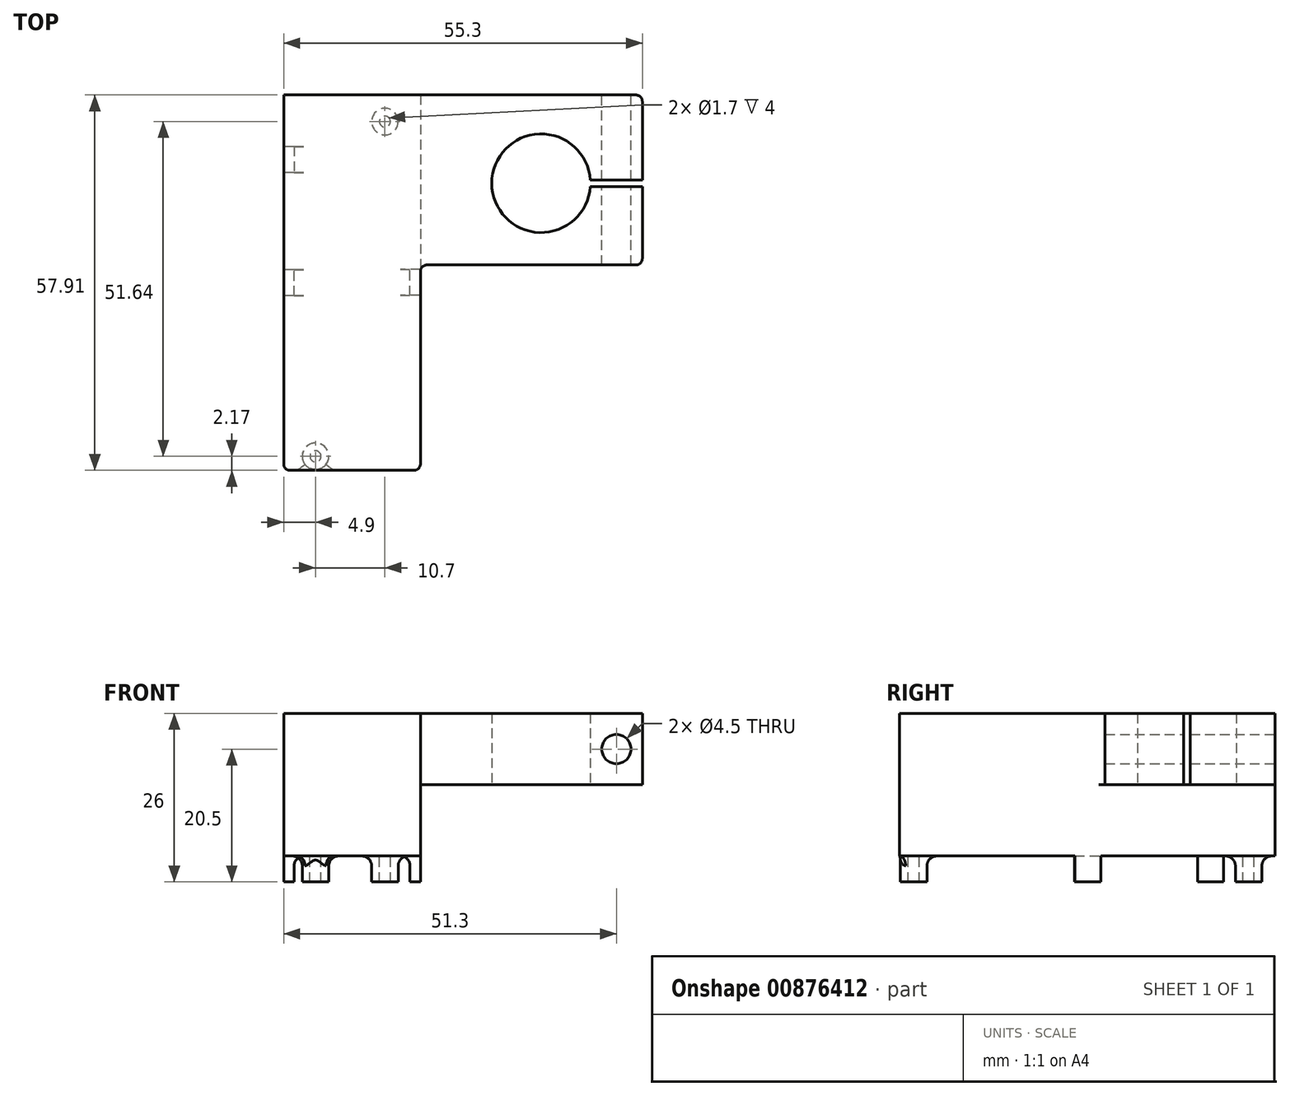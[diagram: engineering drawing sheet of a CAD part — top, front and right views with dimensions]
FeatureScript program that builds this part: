
annotation { "Feature Type Name" : "Feature", "Feature Type Description" : "" }
export const myFeature = defineFeature(function(context is Context, id is Id, definition is map)
    precondition{}
    {
        {
            var Q0;
            Q0=qCreatedBy(makeId("Top.planeOp"),FACE);
            var sketch = newSketch(context, id + "F0", { "sketchPlane" : qUnion([Q0])});
            skCircle(sketch, "E0", {"center": v(0, 0) * mm, "radius": 7.61 * mm});
            skLineSegment(sketch, "E1.bottom", {"start": v(-18.61, 13.61) * mm, "end": v(15.61, 13.61) * mm});
            skLineSegment(sketch, "E1.top", {"start": v(-18.61, -12.6) * mm, "end": v(15.61, -12.6) * mm});
            skLineSegment(sketch, "E1.left", {"start": v(-18.61, 13.61) * mm, "end": v(-18.61, -12.6) * mm});
            skLineSegment(sketch, "E1.right", {"start": v(15.61, 13.61) * mm, "end": v(15.61, -12.6) * mm});
            skLineSegment(sketch, "E2", {"start": v(-18.6, -44.3) * mm, "end": v(-39.69, -44.3) * mm});
            skLineSegment(sketch, "E3", {"start": v(-39.69, -44.3) * mm, "end": v(-39.7, 13.6) * mm});
            skLineSegment(sketch, "E4", {"start": v(-39.7, 13.6) * mm, "end": v(-18.61, 13.6) * mm});
            skLineSegment(sketch, "E5", {"start": v(-18.61, 13.6) * mm, "end": v(-18.61, 13.61) * mm});
            skLineSegment(sketch, "E6", {"start": v(-18.6, -44.3) * mm, "end": v(-18.61, -12.6) * mm});
            skSolve(sketch);
        }
        {
            var Q0;
            {var subQ0=sQuery(id+"F0.wireOp",EDGE,"E2");Q0=makeQuery(id+"F0.imprint","IMPRINT",FACE,{"disambiguationData":[TD([[makeQuery(id+"F0.imprint","IMPRINT",EDGE,{"derivedFrom":subQ0}),-1.0]])]});}
            var Q1;
            Q1=makeQuery(id+"F0.imprint","IMPRINT",FACE,{"disambiguationData":[TD([[makeQuery(id+"F0.imprint","IMPRINT",EDGE,{"derivedFrom":sQuery(id+"F0.wireOp",EDGE,"E0")}),-1.0]])]});
            extrude(context, id + "F1", {"entities" : qUnion([Q0, Q1]), "depth" : 11 * mm, "offsetDistance" : 25 * mm});
        }
        {
            var Q0;
            Q0=makeQuery(id+"F1.opExtrude","CAP_FACE",FACE,{"disambiguationData":[OSD([sQuery(id+"F0.wireOp",EDGE,"E0"),sQuery(id+"F0.wireOp",EDGE,"E1.bottom"),sQuery(id+"F0.wireOp",EDGE,"E1.top"),sQuery(id+"F0.wireOp",EDGE,"E1.left"),sQuery(id+"F0.wireOp",EDGE,"E1.right"),sQuery(id+"F0.wireOp",EDGE,"E2"),sQuery(id+"F0.wireOp",EDGE,"E3"),sQuery(id+"F0.wireOp",EDGE,"E4"),sQuery(id+"F0.wireOp",EDGE,"E5")])],"isStart":true});
            var sketch = newSketch(context, id + "F2", { "sketchPlane" : qUnion([Q0])});
            skLineSegment(sketch, "E7.bottom", {"start": v(-39.7, -13.6) * mm, "end": v(-18.6, -13.6) * mm});
            skLineSegment(sketch, "E7.top", {"start": v(-39.7, 44.3) * mm, "end": v(-18.6, 44.3) * mm});
            skLineSegment(sketch, "E7.left", {"start": v(-39.7, -13.6) * mm, "end": v(-39.7, 44.3) * mm});
            skLineSegment(sketch, "E7.right", {"start": v(-18.6, -13.6) * mm, "end": v(-18.6, 44.3) * mm});
            skSolve(sketch);
        }
        {
            var Q0;
            {var subQ2=sQuery(id+"F2.wireOp",EDGE,"E7.bottom");Q0=makeQuery(id+"F2.imprint","IMPRINT",FACE,{"disambiguationData":[TD([[makeQuery(id+"F2.imprint","IMPRINT",EDGE,{"derivedFrom":subQ2}),1.0]])]});}
            extrude(context, id + "F3", {"entities" : qUnion([Q0]), "operationType" : NewBodyOperationType.ADD, "depth" : (2 + 9) * mm, "offsetDistance" : 25 * mm});
        }
        {
            var Q0;
            Q0=makeQuery(id+"F3.opExtrude","CAP_FACE",FACE,{"disambiguationData":[OSD([sQuery(id+"F2.wireOp",EDGE,"E7.bottom"),sQuery(id+"F2.wireOp",EDGE,"E7.top"),sQuery(id+"F2.wireOp",EDGE,"E7.left"),sQuery(id+"F2.wireOp",EDGE,"E7.right")])],"isStart":false});
            var sketch = newSketch(context, id + "F4", { "sketchPlane" : qUnion([Q0])});
            skCircle(sketch, "E8", {"center": v(-24.09, -9.5) * mm, "radius": 2.05 * mm});
            skCircle(sketch, "E9", {"center": v(-34.79, 42.13) * mm, "radius": 2.05 * mm});
            skCircle(sketch, "E10", {"center": v(-24.09, -9.5) * mm, "radius": 0.85 * mm});
            skCircle(sketch, "E11", {"center": v(-34.79, 42.13) * mm, "radius": 0.85 * mm});
            skLineSegment(sketch, "E12", {"start": v(-33.19, -13.61) * mm, "end": v(-39.7, -3.66) * mm, "construction": true});
            skLineSegment(sketch, "E13", {"start": v(-23.95, -13.6) * mm, "end": v(-18.6, -3.66) * mm, "construction": true});
            skLineSegment(sketch, "E14", {"start": v(-18.6, 35.8) * mm, "end": v(-22.5, 44.3) * mm, "construction": true});
            skLineSegment(sketch, "E15", {"start": v(-23.95, -13.6) * mm, "end": v(-18.6, -13.6) * mm, "construction": true});
            skLineSegment(sketch, "E16", {"start": v(-18.6, -13.6) * mm, "end": v(-18.6, -3.66) * mm, "construction": true});
            skLineSegment(sketch, "E17", {"start": v(-39.69, -3.66) * mm, "end": v(-39.69, -13.6) * mm, "construction": true});
            skLineSegment(sketch, "E18", {"start": v(-39.69, -13.6) * mm, "end": v(-33.19, -13.6) * mm, "construction": true});
            skLineSegment(sketch, "E19", {"start": v(-22.5, 44.3) * mm, "end": v(-18.6, 44.3) * mm, "construction": true});
            skLineSegment(sketch, "E20", {"start": v(-18.6, 44.3) * mm, "end": v(-18.6, 35.8) * mm, "construction": true});
            skLineSegment(sketch, "E21.bottom", {"start": v(-38.09, 17.35) * mm, "end": v(-39.69, 17.35) * mm});
            skLineSegment(sketch, "E21.top", {"start": v(-38.09, 13.35) * mm, "end": v(-39.69, 13.35) * mm});
            skLineSegment(sketch, "E21.left", {"start": v(-38.09, 17.35) * mm, "end": v(-38.09, 13.35) * mm});
            skLineSegment(sketch, "E21.right", {"start": v(-39.69, 17.35) * mm, "end": v(-39.69, 13.35) * mm});
            skLineSegment(sketch, "E22.bottom", {"start": v(-18.6, 17.3) * mm, "end": v(-20.2, 17.3) * mm});
            skLineSegment(sketch, "E22.top", {"start": v(-18.6, 13.3) * mm, "end": v(-20.2, 13.3) * mm});
            skLineSegment(sketch, "E22.left", {"start": v(-18.6, 17.3) * mm, "end": v(-18.6, 13.3) * mm});
            skLineSegment(sketch, "E22.right", {"start": v(-20.2, 17.3) * mm, "end": v(-20.2, 13.3) * mm});
            skPoint(sketch, "E23", {"position": v(-39.69, 15.35) * mm});
            skPoint(sketch, "E24", {"position": v(-18.6, 15.35) * mm});
            skPoint(sketch, "E25", {"position": v(-18.6, -3.66) * mm});
            skLineSegment(sketch, "E26.bottom", {"start": v(-38.1, -5.66) * mm, "end": v(-39.7, -5.66) * mm});
            skLineSegment(sketch, "E26.top", {"start": v(-38.1, -1.66) * mm, "end": v(-39.7, -1.66) * mm});
            skLineSegment(sketch, "E26.left", {"start": v(-38.1, -5.66) * mm, "end": v(-38.1, -1.66) * mm});
            skLineSegment(sketch, "E26.right", {"start": v(-39.7, -5.66) * mm, "end": v(-39.7, -1.66) * mm});
            skPoint(sketch, "E27", {"position": v(-39.69, -3.66) * mm});
            skSolve(sketch);
        }
        {
            var Q0;
            Q0=makeQuery(id+"F4.imprint","IMPRINT",FACE,{"disambiguationData":[TD([[makeQuery(id+"F4.imprint","IMPRINT",EDGE,{"derivedFrom":sQuery(id+"F4.wireOp",EDGE,"E9")}),1.0]])]});
            var Q1;
            Q1=makeQuery(id+"F4.imprint","IMPRINT",FACE,{"disambiguationData":[TD([[makeQuery(id+"F4.imprint","IMPRINT",EDGE,{"derivedFrom":sQuery(id+"F4.wireOp",EDGE,"E8")}),1.0]])]});
            var Q2;
            Q2=makeQuery(id+"F4.imprint","IMPRINT",FACE,{"disambiguationData":[TD([[makeQuery(id+"F4.imprint","IMPRINT",EDGE,{"derivedFrom":sQuery(id+"F4.wireOp",EDGE,"E22.bottom")}),1.0]])]});
            var Q3;
            Q3=makeQuery(id+"F4.imprint","IMPRINT",FACE,{"disambiguationData":[TD([[makeQuery(id+"F4.imprint","IMPRINT",EDGE,{"derivedFrom":sQuery(id+"F4.wireOp",EDGE,"E21.bottom")}),1.0]])]});
            var Q4;
            Q4=makeQuery(id+"F4.imprint","IMPRINT",FACE,{"disambiguationData":[TD([[makeQuery(id+"F4.imprint","IMPRINT",EDGE,{"derivedFrom":sQuery(id+"F4.wireOp",EDGE,"J9qzsF46-yFWu-7e5G-CuOQ-CInMZGLrBgDS.bottom")}),1.0]])]});
            var Q5;
            Q5=makeQuery(id+"F4.imprint","IMPRINT",FACE,{"disambiguationData":[TD([[makeQuery(id+"F4.imprint","IMPRINT",EDGE,{"derivedFrom":sQuery(id+"F4.wireOp",EDGE,"E26.bottom")}),-1.0]])]});
            extrude(context, id + "F5", {"entities" : qUnion([Q0, Q1, Q2, Q3, Q4, Q5]), "operationType" : NewBodyOperationType.ADD, "depth" : 4 * mm, "offsetDistance" : 25 * mm});
        }
        {
            var Q0;
            Q0=makeQuery(id+"F1.opExtrude","SWEPT_FACE",FACE,{"disambiguationData":[OSD([sQuery(id+"F0.wireOp",EDGE,"E1.right")])]});
            var sketch = newSketch(context, id + "F6", { "sketchPlane" : qUnion([Q0])});
            skLineSegment(sketch, "E28.bottom", {"start": v(-0.5, 0) * mm, "end": v(0.5, 0) * mm});
            skLineSegment(sketch, "E28.top", {"start": v(-0.5, 11) * mm, "end": v(0.5, 11) * mm});
            skLineSegment(sketch, "E28.left", {"start": v(-0.5, 0) * mm, "end": v(-0.5, 11) * mm});
            skLineSegment(sketch, "E28.right", {"start": v(0.5, 0) * mm, "end": v(0.5, 11) * mm});
            skSolve(sketch);
        }
        {
            var Q0;
            Q0=makeQuery(id+"F6.imprint","IMPRINT",FACE,{"disambiguationData":[TD([[makeQuery(id+"F6.imprint","IMPRINT",EDGE,{"derivedFrom":sQuery(id+"F6.wireOp",EDGE,"E28.bottom")}),-1.0]])]});
            extrude(context, id + "F7", {"entities" : qUnion([Q0]), "operationType" : NewBodyOperationType.REMOVE, "endBound" : BoundingType.UP_TO_NEXT, "oppositeDirection" : true, "depth" : 25 * mm, "offsetDistance" : 25 * mm});
        }
        {
            var Q0;
            Q0=makeQuery(id+"F1.opExtrude","SWEPT_FACE",FACE,{"disambiguationData":[OSD([sQuery(id+"F0.wireOp",EDGE,"E1.bottom")])]});
            var sketch = newSketch(context, id + "F8", { "sketchPlane" : qUnion([Q0])});
            skCircle(sketch, "E29", {"center": v(-11.61, 5.5) * mm, "radius": 2.25 * mm});
            skSolve(sketch);
        }
        {
            var Q0;
            Q0=makeQuery(id+"F8.imprint","IMPRINT",FACE,{"disambiguationData":[TD([[makeQuery(id+"F8.imprint","IMPRINT",EDGE,{"derivedFrom":sQuery(id+"F8.wireOp",EDGE,"E29")}),1.0]])]});
            extrude(context, id + "F9", {"entities" : qUnion([Q0]), "operationType" : NewBodyOperationType.REMOVE, "endBound" : BoundingType.THROUGH_ALL, "oppositeDirection" : true, "depth" : 25 * mm, "offsetDistance" : 25 * mm});
        }
        {
            var Q0;
            Q0=makeQuery(id+"F5.opExtrude","CAP_EDGE",EDGE,{"disambiguationData":[OSD([sQuery(id+"F4.wireOp",EDGE,"E9")])],"isStart":true});
            var Q1;
            Q1=makeQuery(id+"F5.opExtrude","CAP_EDGE",EDGE,{"disambiguationData":[OSD([sQuery(id+"F4.wireOp",EDGE,"E8")])],"isStart":true});
            var Q2;
            Q2=makeQuery(id+"F5.opExtrude","CAP_EDGE",EDGE,{"disambiguationData":[OSD([sQuery(id+"F4.wireOp",EDGE,"E22.right")])],"isStart":true});
            var Q3;
            Q3=makeQuery(id+"F5.opExtrude","CAP_EDGE",EDGE,{"disambiguationData":[OSD([sQuery(id+"F4.wireOp",EDGE,"E21.left")])],"isStart":true});
            var Q4;
            Q4=makeQuery(id+"F5.opExtrude","CAP_EDGE",EDGE,{"disambiguationData":[OSD([sQuery(id+"F4.wireOp",EDGE,"J9qzsF46-yFWu-7e5G-CuOQ-CInMZGLrBgDS.left")])],"isStart":true});
            var Q5;
            Q5=makeQuery(id+"F5.opExtrude","CAP_EDGE",EDGE,{"disambiguationData":[OSD([sQuery(id+"F4.wireOp",EDGE,"E26.left")])],"isStart":true});
            fillet(context, id + "F10", {"entities" : qUnion([Q0, Q1, Q2, Q3, Q4, Q5]), "radius" : 1.5 * mm, "tangentPropagation" : true, "defaultsChanged" : false, "vertexSettings" : [], "allowEdgeOverflow" : false});
        }
        {
            var Q0;
            Q0=makeQuery(id+"F1.opExtrude","SWEPT_EDGE",EDGE,{"disambiguationData":[OSD([sQuery(id+"F0.wireOp",EDGE,"E1.left"),sQuery(id+"F0.wireOp",EDGE,"E2")])]});
            var Q1;
            Q1=makeQuery(id+"F1.opExtrude","SWEPT_EDGE",EDGE,{"disambiguationData":[OSD([sQuery(id+"F0.wireOp",EDGE,"E1.top"),sQuery(id+"F0.wireOp",EDGE,"E1.left")])]});
            var Q2;
            Q2=makeQuery(id+"F1.opExtrude","SWEPT_EDGE",EDGE,{"disambiguationData":[OSD([sQuery(id+"F0.wireOp",EDGE,"E1.top"),sQuery(id+"F0.wireOp",EDGE,"E1.right")])]});
            var Q3;
            Q3=makeQuery(id+"F1.opExtrude","SWEPT_EDGE",EDGE,{"disambiguationData":[OSD([sQuery(id+"F0.wireOp",EDGE,"E1.bottom"),sQuery(id+"F0.wireOp",EDGE,"E1.right")])]});
            fillet(context, id + "F11", {"entities" : qUnion([Q0, Q1, Q2, Q3]), "radius" : 1 * mm, "tangentPropagation" : true, "allowEdgeOverflow" : false});
        }
    });
